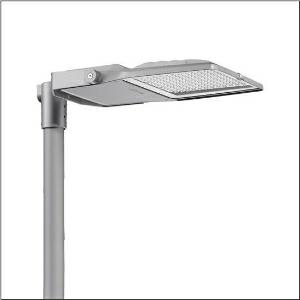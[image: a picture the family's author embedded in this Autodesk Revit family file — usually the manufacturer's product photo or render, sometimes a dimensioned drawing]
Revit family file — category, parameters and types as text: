
# Revit family: floodlight_fl_21_midi___pl43_5xa7782e2a3a_7ebc
name_source: partatom
category: Lighting Fixtures
units: mm (PartAtom-declared; Revit-internal decimal feet)

## family parameters
Cut with Voids When Loaded = No
Host = Face
Light Source = No
Part Type = Normal
Room Calculation Point = No
Round Connector Dimension = Use Diameter
Shared = No

## types (1)
- --- (1 x LED, 27540 lm, 208.1 W, 3000K)
    Apparent Load = 208 VA
    CIE Flux Codes = 27 78 99 100 100
    Color Rendering = 70
    Color Temperature = 3000K
    Default Elevation = 1800 mm
    Description = Floodlight FL 21 midi, floodlight, primary light control with lens, of PMMA, primary optical cover: protective disc, of toughened safety glass, transparent, light distribution: PL43, light emission: direct distribution, installation type: surface-mounted, LED, High Power LED, rated luminous flux: 27.540lm, luminous efficacy: 132lm/W, light colour: 730, colour temperature: 3000K, control gear: ECG iQ, control: optimised constant luminous flux control (CLO 2.0), Desk-Remote (wireless, voltage-free reading and setting of iQ features in the workshop via application-optimized NFC function/RFID function), Smart-Wire, Night-Set, Temp-Guard, Auto-Match, Street-Remote, with terminal, 6-pole, mains connection: 220..240V, AC, 50/60Hz, start of lifetime: 208W, end of lifetime: 227W, reduction: 90W, luminaire housing, of diecast aluminium, powder-coated, Siteco® metallic grey (DB 702S), corrosivity category C5 according to DIN EN ISO 12944, mast bracket, of steel, galvanised, powder-coated, Siteco® metallic grey (DB 702S), protection rating (complete): IP66, insulation class (complete): insulation class II (safety insulation), certification: CE, protection symbol: D, impact resistance: IK08, permissible operating ambient temperature: -40..+40°C, permissible operating ambient temperature for outdoor applications: -40..+50°C, standard: DIN EN 12944, packaging unit: 1 piece

Light Distribution: PL43
    Height = 76 mm
    Lamp = 1 x LED
    Lamp Light Flux = 27540 lm
    Lamp Power = 208.1 W
    Lamp count = 1
    Length = 657 mm
    Luminous efficacy = 132 lm/W
    Manufacturer = Siteco
    ModVariant = No
    Model = 5XA7782E2A3A
    Number of Poles = 1
    OnlyDefault = Yes
    Power Factor = 1
    Product Name = Floodlight FL 21 midi | PL43
    Product group = floodlight | pylon top
    ProductGroupID = 6101
    Protection Class = Protection class II
    Protection Degree = IP 66
    RLX_Detail_Level = 1
    RlxData = <blob elided: 153281 chars, md5=2cff9315>
    Socket = socket
    Standby Power = 0 W
    System Light Flux = 27540 lm
    System Power = 208 W
    Type Comments = factory setting: luminous flux: 100 % | dim-lin: 254 | 710 mA
    Type Image = l_1007123.jpg
    URL = http://relux.com
    VarID = @adj_013791
    Voltage = 0 V
    Weight = 0.00 kg
    Width = 442 mm

## geometry (parser evidence)
native form markers: Blend x4, Sweep x13
no freeform markers — native parametric forms only
